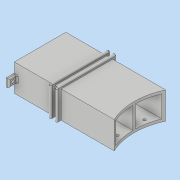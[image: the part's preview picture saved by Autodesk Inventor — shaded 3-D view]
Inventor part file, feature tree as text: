
AUTODESK INVENTOR PART (.ipt)
format: ipt  version: 2019 (Build 230136000, 136)  size: 594,944 bytes
history: native  units: mm
features: sketch x20, extrude x19, projected_geometry x8, other x4, fillet x2, loft x1, shell x1
ambient origin geometry x8: Origin, YZ Plane, XZ Plane, XY Plane, X Axis, Y Axis, Z Axis, Center Point
bodies: Body1 (feature_tree), Body2 (feature_tree), Body3 (feature_tree), Body4 (feature_tree)
feature tree (55):
  other  "хребет2"
  sketch  "Эскиз4"
  other  "РабПлоскость1"
  sketch  "Эскиз5"
  loft  "Лофт1"
  extrude  "Выдавливание2"  Depth=100.0mm
  shell  "Оболочка1"  Thickness=17.0mm
  sketch  "Эскиз21"
  extrude  "Выдавливание16"  Depth=4.0mm
  extrude  "Выдавливание98"  Depth=35.0mm
  extrude  "Выдавливание99"  TaperAngle=0.0deg  [1 undecoded]
  extrude  "Выдавливание100"  TaperAngle=0.0deg  [1 undecoded]
  extrude  "Выдавливание101"  TaperAngle=0.0deg  [1 undecoded]
  extrude  "Выдавливание102"  Depth=130.0mm TaperAngle=0.0deg
  extrude  "Выдавливание103"  Depth=5.0mm
  extrude  "Выдавливание104"  Depth=2.0mm
  extrude  "Выдавливание105"  Depth=2.0mm
  extrude  "Выдавливание106"  Depth=10.0mm TaperAngle=0.0deg
  fillet  "Сопряжение4"  Radius=2.0mm
  extrude  "Выдавливание107"  Depth=37.306mm
  extrude  "Выдавливание108"  Depth=5.0mm
  fillet  "Сопряжение5"  Radius=10.0mm
  other  "РабПлоскость25"
  sketch  "Эскиз125"
  extrude  "Выдавливание109"  Depth=38.0mm
  extrude  "Выдавливание110"  Depth=20.0mm
  extrude  "Выдавливание111"  Depth=2.0mm
  extrude  "Выдавливание112"  Depth=2.0mm
  other  "РабПлоскость26"
  extrude  "Выдавливание113"  Depth=2.0mm
  extrude  "Выдавливание114"  Depth=10.0mm TaperAngle=0.0deg
  sketch  "Эскиз6"
  projected_geometry  "Спроецированная петля1"
  sketch  "Эскиз114"
  sketch  "Эскиз115"
  sketch  "Эскиз116"
  sketch  "Эскиз117"
  sketch  "Эскиз118"
  projected_geometry  "Спроецированная петля45"
  sketch  "Эскиз119"
  sketch  "Эскиз120"
  sketch  "Эскиз121"
  projected_geometry  "Спроецированная петля46"
  sketch  "Эскиз122"
  projected_geometry  "Спроецированная петля47"
  projected_geometry  "Спроецированная петля48"
  sketch  "Эскиз123"
  sketch  "Эскиз124"
  projected_geometry  "Спроецированная петля49"
  projected_geometry  "Спроецированная петля50"
  sketch  "Эскиз126"
  sketch  "Эскиз127"
  projected_geometry  "Спроецированная петля51"
  sketch  "Эскиз128"
  sketch  "Эскиз129"
note: 3 required parameter values undecoded (feature->parameter linkage not recoverable at this tier; creation-order binding heuristic only, values carry confidence <= 0.55)
